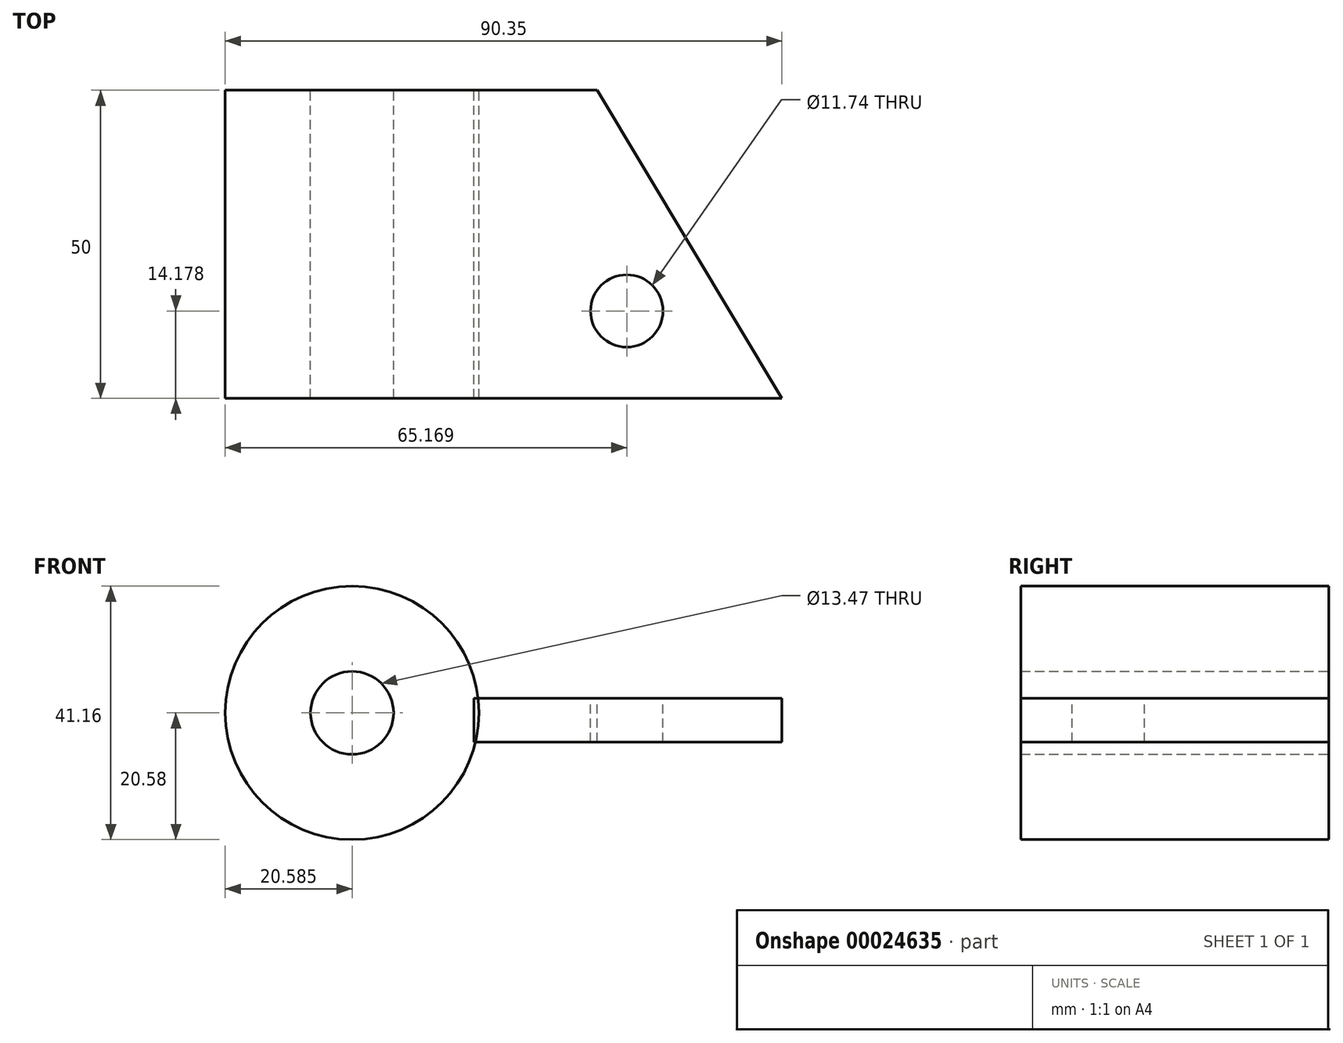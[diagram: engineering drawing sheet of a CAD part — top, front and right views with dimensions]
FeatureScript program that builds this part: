
annotation { "Feature Type Name" : "Feature", "Feature Type Description" : "" }
export const myFeature = defineFeature(function(context is Context, id is Id, definition is map)
    precondition{}
    {
        {
            var Q0;
            Q0=qCreatedBy(makeId("Front.planeOp"),FACE);
            var sketch = newSketch(context, id + "F0", { "sketchPlane" : qUnion([Q0])});
            skCircle(sketch, "E0", {"center": v(-44.76, 6.82) * mm, "radius": 20.58 * mm});
            skCircle(sketch, "E1", {"center": v(-44.76, 6.82) * mm, "radius": 6.74 * mm});
            skSolve(sketch);
        }
        {
            var Q0;
            Q0=makeQuery(id+"F0.imprint","IMPRINT",FACE,{"disambiguationData":[TD([[makeQuery(id+"F0.imprint","IMPRINT",EDGE,{"derivedFrom":sQuery(id+"F0.wireOp",EDGE,"E0")}),1.0]])]});
            extrude(context, id + "F1", {"entities" : qUnion([Q0]), "depth" : 50 * mm});
        }
        {
            var Q0;
            Q0=qCreatedBy(makeId("Right.planeOp"),FACE);
            var sketch = newSketch(context, id + "F2", { "sketchPlane" : qUnion([Q0])});
            skLineSegment(sketch, "E2.bottom", {"start": v(-50.14, 9.18) * mm, "end": v(0, 9.18) * mm});
            skLineSegment(sketch, "E2.top", {"start": v(-50.14, 2.1) * mm, "end": v(0, 2.1) * mm});
            skLineSegment(sketch, "E2.left", {"start": v(-50.14, 9.18) * mm, "end": v(-50.14, 2.1) * mm});
            skLineSegment(sketch, "E2.right", {"start": v(0, 9.18) * mm, "end": v(0, 2.1) * mm});
            skSolve(sketch);
        }
        {
            var Q0;
            Q0=makeQuery(id+"F2.imprint","IMPRINT",FACE,{"disambiguationData":[TD([[makeQuery(id+"F2.imprint","IMPRINT",EDGE,{"derivedFrom":sQuery(id+"F2.wireOp",EDGE,"E2.bottom")}),-1.0]])]});
            extrude(context, id + "F3", {"entities" : qUnion([Q0]), "oppositeDirection" : true, "depth" : 25 * mm});
        }
        {
            var Q0;
            Q0=makeQuery(id+"F3.opExtrude","CAP_FACE",FACE,{"disambiguationData":[OSD([sQuery(id+"F2.wireOp",EDGE,"E2.bottom"),sQuery(id+"F2.wireOp",EDGE,"E2.top"),sQuery(id+"F2.wireOp",EDGE,"E2.left"),sQuery(id+"F2.wireOp",EDGE,"E2.right")])],"isStart":true});
            extrude(context, id + "F4", {"entities" : qUnion([Q0]), "operationType" : NewBodyOperationType.ADD, "depth" : 25 * mm});
        }
        {
            var Q0;
            {var subQ0=sQuery(id+"F2.wireOp",EDGE,"E2.left");Q0=makeQuery(id+"F4.boolean.opBoolean","MERGE",FACE,{"derivedFrom":[makeQuery(id+"F3.opExtrude","SWEPT_FACE",FACE,{"disambiguationData":[OSD([subQ0])]}),makeQuery(id+"F4.opExtrude","SWEPT_FACE",FACE,{"disambiguationData":[OSD([subQ0])]})]});}
            var Q1;
            Q1=makeQuery(id+"F1.opExtrude","CAP_FACE",FACE,{"disambiguationData":[OSD([sQuery(id+"F0.wireOp",EDGE,"E0"),sQuery(id+"F0.wireOp",EDGE,"E1")])],"isStart":false});
            extrude(context, id + "F5", {"entities" : qUnion([Q0]), "operationType" : NewBodyOperationType.REMOVE, "endBound" : BoundingType.UP_TO_SURFACE, "oppositeDirection" : true, "endBoundEntityFace" : qUnion([Q1]), "depth" : 25 * mm});
        }
        {
            var Q0;
            {var subQ0=sQuery(id+"F2.wireOp",EDGE,"E2.bottom");Q0=makeQuery(id+"F4.boolean.opBoolean","MERGE",FACE,{"derivedFrom":[makeQuery(id+"F3.opExtrude","SWEPT_FACE",FACE,{"disambiguationData":[OSD([subQ0])]}),makeQuery(id+"F4.opExtrude","SWEPT_FACE",FACE,{"disambiguationData":[OSD([subQ0])]})]});}
            var sketch = newSketch(context, id + "F6", { "sketchPlane" : qUnion([Q0])});
            skLineSegment(sketch, "E3", {"start": v(25, -50) * mm, "end": v(-4.96, 0) * mm});
            skSolve(sketch);
        }
        {
            var Q0;
            {var subQ3=sQuery(id+"F6.wireOp",EDGE,"E3");Q0=makeQuery(id+"F6.imprint","IMPRINT",FACE,{"disambiguationData":[TD([[makeQuery(id+"F6.imprint","IMPRINT",EDGE,{"derivedFrom":subQ3}),-1.0]])]});}
            extrude(context, id + "F7", {"entities" : qUnion([Q0]), "operationType" : NewBodyOperationType.REMOVE, "endBound" : BoundingType.THROUGH_ALL, "oppositeDirection" : true, "depth" : 25 * mm});
        }
        {
            var Q0;
            {var subQ0=sQuery(id+"F2.wireOp",EDGE,"E2.bottom");Q0=makeQuery(id+"F4.boolean.opBoolean","MERGE",FACE,{"derivedFrom":[makeQuery(id+"F3.opExtrude","SWEPT_FACE",FACE,{"disambiguationData":[OSD([subQ0])]}),makeQuery(id+"F4.opExtrude","SWEPT_FACE",FACE,{"disambiguationData":[OSD([subQ0])]})]});}
            var sketch = newSketch(context, id + "F8", { "sketchPlane" : qUnion([Q0])});
            skCircle(sketch, "E4", {"center": v(-0.18, -35.82) * mm, "radius": 5.87 * mm});
            skSolve(sketch);
        }
        {
            var Q0;
            Q0=makeQuery(id+"F8.imprint","IMPRINT",FACE,{"disambiguationData":[TD([[makeQuery(id+"F8.imprint","IMPRINT",EDGE,{"derivedFrom":sQuery(id+"F8.wireOp",EDGE,"E4")}),1.0]])]});
            extrude(context, id + "F9", {"entities" : qUnion([Q0]), "operationType" : NewBodyOperationType.REMOVE, "endBound" : BoundingType.THROUGH_ALL, "oppositeDirection" : true, "depth" : 25 * mm});
        }
    });
